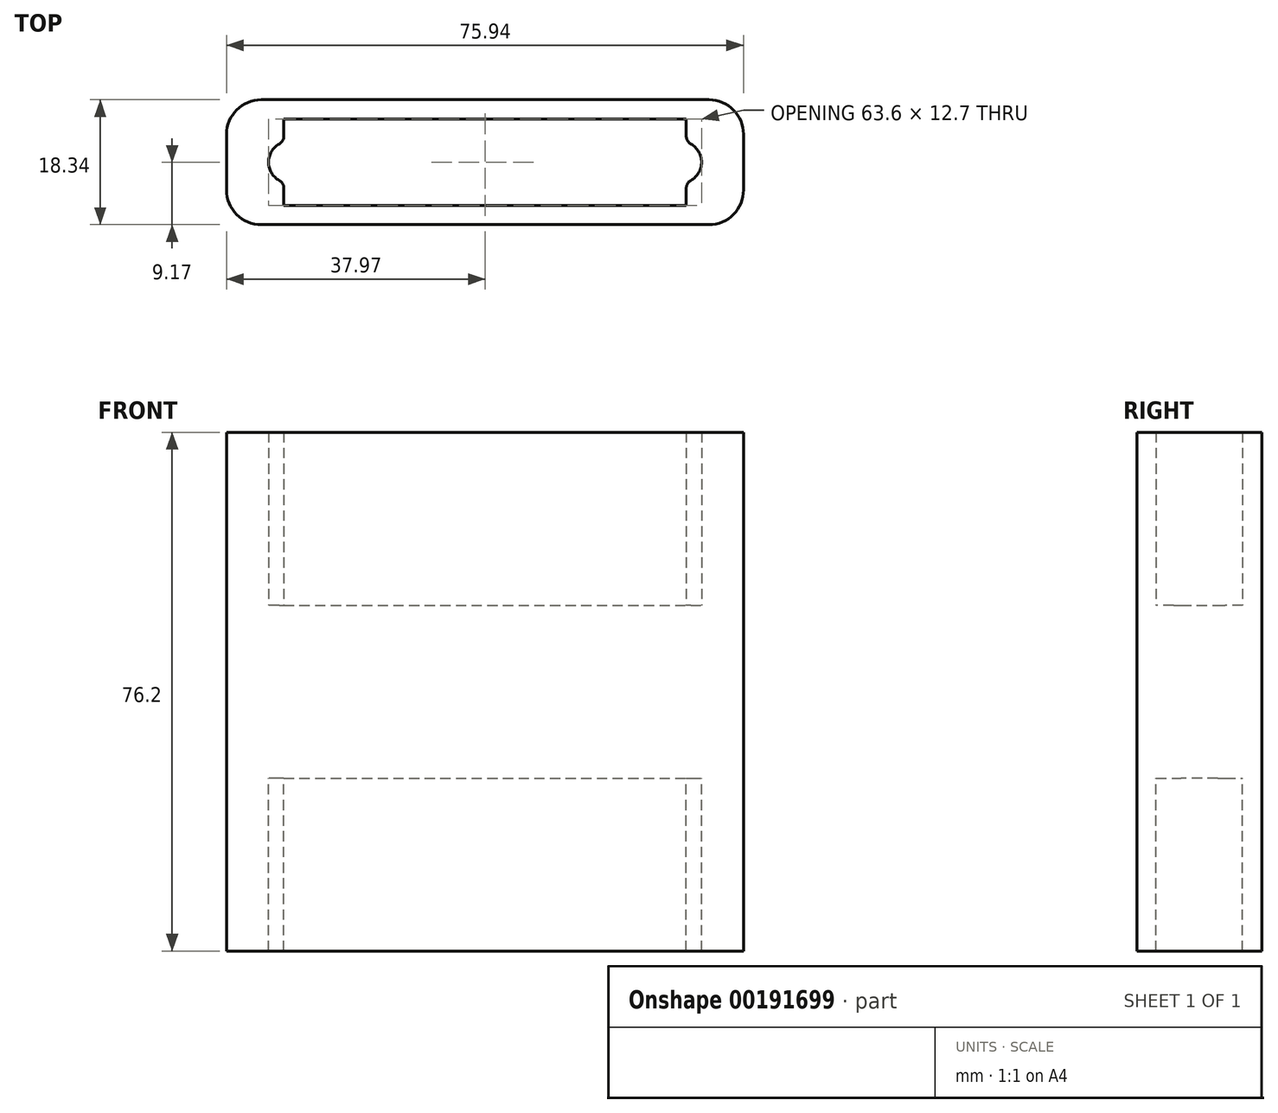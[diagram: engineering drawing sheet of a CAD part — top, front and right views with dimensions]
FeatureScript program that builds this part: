
annotation { "Feature Type Name" : "Feature", "Feature Type Description" : "" }
export const myFeature = defineFeature(function(context is Context, id is Id, definition is map)
    precondition{}
    {
        {
            var Q0;
            Q0=qCreatedBy(makeId("Top.planeOp"),FACE);
            var sketch = newSketch(context, id + "F0", { "sketchPlane" : qUnion([Q0])});
            skLineSegment(sketch, "E0.bottom", {"start": v(-37.97, 9.17) * mm, "end": v(37.97, 9.17) * mm});
            skLineSegment(sketch, "E0.top", {"start": v(-37.97, -9.17) * mm, "end": v(37.97, -9.17) * mm});
            skLineSegment(sketch, "E0.left", {"start": v(-37.97, 9.17) * mm, "end": v(-37.97, -9.17) * mm});
            skLineSegment(sketch, "E0.right", {"start": v(37.97, 9.17) * mm, "end": v(37.97, -9.17) * mm});
            skSolve(sketch);
        }
        {
            var Q0;
            Q0 = qSketchRegion(id + "F0", true);
            extrude(context, id + "F1", {"entities" : qUnion([Q0]), "endBound" : BoundingType.SYMMETRIC, "depth" : 25.4 * mm});
        }
        {
            var Q0;
            Q0=makeQuery(id+"F1.opExtrude","CAP_FACE",FACE,{"disambiguationData":[OSD([sQuery(id+"F0.wireOp",EDGE,"E0.bottom"),sQuery(id+"F0.wireOp",EDGE,"E0.top"),sQuery(id+"F0.wireOp",EDGE,"E0.left"),sQuery(id+"F0.wireOp",EDGE,"E0.right")])],"isStart":false});
            var sketch = newSketch(context, id + "F2", { "sketchPlane" : qUnion([Q0])});
            skLineSegment(sketch, "E1.bottom", {"start": v(-29.57, 6.35) * mm, "end": v(29.57, 6.35) * mm});
            skLineSegment(sketch, "E1.top", {"start": v(-29.57, -6.35) * mm, "end": v(29.57, -6.35) * mm});
            skLineSegment(sketch, "E1.left", {"start": v(-29.57, 6.35) * mm, "end": v(-29.57, 2.96) * mm});
            skLineSegment(sketch, "E1.right", {"start": v(29.57, 6.35) * mm, "end": v(29.57, 2.96) * mm});
            skPoint(sketch, "E2", {"position": v(-28.73, 0) * mm});
            skArc(sketch, "E3", {"start": v(-29.57, 2.96) * mm, "mid": v(-31.8, 0) * mm, "end": v(-29.57, -2.96) * mm});
            skLineSegment(sketch, "E4.trimOffspring", {"start": v(-29.57, -2.96) * mm, "end": v(-29.57, -6.35) * mm});
            skPoint(sketch, "E5", {"position": v(28.73, 0) * mm});
            skPoint(sketch, "E5.positionSnap0", {"position": v(29.57, 0) * mm});
            skArc(sketch, "E6", {"start": v(29.57, -2.96) * mm, "mid": v(31.8, 0) * mm, "end": v(29.57, 2.96) * mm});
            skLineSegment(sketch, "E7.trimOffspring", {"start": v(29.57, -2.96) * mm, "end": v(29.57, -6.35) * mm});
            skSolve(sketch);
        }
        {
            var Q0;
            Q0=makeQuery(id+"F1.opExtrude","CAP_FACE",FACE,{"disambiguationData":[OSD([sQuery(id+"F0.wireOp",EDGE,"E0.bottom"),sQuery(id+"F0.wireOp",EDGE,"E0.top"),sQuery(id+"F0.wireOp",EDGE,"E0.left"),sQuery(id+"F0.wireOp",EDGE,"E0.right")])],"isStart":true});
            var sketch = newSketch(context, id + "F3", { "sketchPlane" : qUnion([Q0])});
            skLineSegment(sketch, "E8.bottom", {"start": v(-29.57, 6.35) * mm, "end": v(29.57, 6.35) * mm});
            skLineSegment(sketch, "E8.top", {"start": v(-29.57, -6.35) * mm, "end": v(29.57, -6.35) * mm});
            skLineSegment(sketch, "E8.left", {"start": v(-29.57, 6.35) * mm, "end": v(-29.57, 2.96) * mm});
            skLineSegment(sketch, "E8.right", {"start": v(29.57, 6.35) * mm, "end": v(29.57, 2.96) * mm});
            skPoint(sketch, "E9", {"position": v(-28.73, 0) * mm});
            skArc(sketch, "E10", {"start": v(-29.57, 2.96) * mm, "mid": v(-31.8, 0) * mm, "end": v(-29.57, -2.96) * mm});
            skLineSegment(sketch, "E11.trimOffspring", {"start": v(-29.57, -2.96) * mm, "end": v(-29.57, -6.35) * mm});
            skPoint(sketch, "E12", {"position": v(28.73, 0) * mm});
            skPoint(sketch, "E12.positionSnap0", {"position": v(29.57, 0) * mm});
            skArc(sketch, "E13", {"start": v(29.57, -2.96) * mm, "mid": v(31.8, 0) * mm, "end": v(29.57, 2.96) * mm});
            skLineSegment(sketch, "E14.trimOffspring", {"start": v(29.57, -2.96) * mm, "end": v(29.57, -6.35) * mm});
            skSolve(sketch);
        }
        {
            var Q0;
            Q0=makeQuery(id+"F2.imprint","IMPRINT",FACE,{"disambiguationData":[TD([[makeQuery(id+"F2.imprint","IMPRINT",EDGE,{"derivedFrom":sQuery(id+"F2.wireOp",EDGE,"E1.bottom")}),1.0]])]});
            extrude(context, id + "F4", {"entities" : qUnion([Q0]), "operationType" : NewBodyOperationType.ADD, "depth" : 25.4 * mm});
        }
        {
            var Q0;
            Q0=makeQuery(id+"F3.imprint","IMPRINT",FACE,{"disambiguationData":[TD([[makeQuery(id+"F3.imprint","IMPRINT",EDGE,{"derivedFrom":sQuery(id+"F3.wireOp",EDGE,"E8.bottom")}),1.0]])]});
            extrude(context, id + "F5", {"entities" : qUnion([Q0]), "operationType" : NewBodyOperationType.ADD, "depth" : 25.4 * mm});
        }
        {
            var Q0;
            Q0=makeQuery(id+"F4.opExtrude","SWEPT_EDGE",EDGE,{"disambiguationData":[OSD([sQuery(id+"F2.wireOp",EDGE,"E1.left"),sQuery(id+"F2.wireOp",EDGE,"E3")])]});
            var Q1;
            Q1=makeQuery(id+"F4.opExtrude","SWEPT_EDGE",EDGE,{"disambiguationData":[OSD([sQuery(id+"F2.wireOp",EDGE,"E3"),sQuery(id+"F2.wireOp",EDGE,"E4.trimOffspring")])]});
            var Q2;
            Q2=makeQuery(id+"F4.opExtrude","SWEPT_EDGE",EDGE,{"disambiguationData":[OSD([sQuery(id+"F2.wireOp",EDGE,"E6"),sQuery(id+"F2.wireOp",EDGE,"E7.trimOffspring")])]});
            var Q3;
            Q3=makeQuery(id+"F4.opExtrude","SWEPT_EDGE",EDGE,{"disambiguationData":[OSD([sQuery(id+"F2.wireOp",EDGE,"E1.right"),sQuery(id+"F2.wireOp",EDGE,"E6")])]});
            var Q4;
            Q4=makeQuery(id+"F5.opExtrude","SWEPT_EDGE",EDGE,{"disambiguationData":[OSD([sQuery(id+"F3.wireOp",EDGE,"E8.left"),sQuery(id+"F3.wireOp",EDGE,"E10")])]});
            var Q5;
            Q5=makeQuery(id+"F5.opExtrude","SWEPT_EDGE",EDGE,{"disambiguationData":[OSD([sQuery(id+"F3.wireOp",EDGE,"E10"),sQuery(id+"F3.wireOp",EDGE,"E11.trimOffspring")])]});
            var Q6;
            Q6=makeQuery(id+"F5.opExtrude","SWEPT_EDGE",EDGE,{"disambiguationData":[OSD([sQuery(id+"F3.wireOp",EDGE,"E13"),sQuery(id+"F3.wireOp",EDGE,"E14.trimOffspring")])]});
            var Q7;
            Q7=makeQuery(id+"F5.opExtrude","SWEPT_EDGE",EDGE,{"disambiguationData":[OSD([sQuery(id+"F3.wireOp",EDGE,"E8.right"),sQuery(id+"F3.wireOp",EDGE,"E13")])]});
            fillet(context, id + "F6", {"entities" : qUnion([Q0, Q1, Q2, Q3, Q4, Q5, Q6, Q7]), "radius" : 1.27 * mm, "tangentPropagation" : true, "allowEdgeOverflow" : false});
        }
        {
            var Q0;
            {var subQ0=sQuery(id+"F0.wireOp",EDGE,"E0.right");var subQ1=sQuery(id+"F0.wireOp",EDGE,"E0.top");Q0=makeQuery(id+"F5.boolean.opBoolean","MERGE",EDGE,{"derivedFrom":[makeQuery(id+"F4.boolean.opBoolean","MERGE",EDGE,{"derivedFrom":[makeQuery(id+"F1.opExtrude","SWEPT_EDGE",EDGE,{"disambiguationData":[OSD([subQ1,subQ0])]}),makeQuery(id+"F4.opExtrude","SWEPT_EDGE",EDGE,{"disambiguationData":[OSD([subQ1,subQ0])]})]}),makeQuery(id+"F5.opExtrude","SWEPT_EDGE",EDGE,{"disambiguationData":[OSD([subQ1,subQ0])]})]});}
            var Q1;
            {var subQ0=sQuery(id+"F0.wireOp",EDGE,"E0.right");var subQ1=sQuery(id+"F0.wireOp",EDGE,"E0.bottom");Q1=makeQuery(id+"F5.boolean.opBoolean","MERGE",EDGE,{"derivedFrom":[makeQuery(id+"F4.boolean.opBoolean","MERGE",EDGE,{"derivedFrom":[makeQuery(id+"F1.opExtrude","SWEPT_EDGE",EDGE,{"disambiguationData":[OSD([subQ1,subQ0])]}),makeQuery(id+"F4.opExtrude","SWEPT_EDGE",EDGE,{"disambiguationData":[OSD([subQ1,subQ0])]})]}),makeQuery(id+"F5.opExtrude","SWEPT_EDGE",EDGE,{"disambiguationData":[OSD([subQ1,subQ0])]})]});}
            var Q2;
            {var subQ0=sQuery(id+"F0.wireOp",EDGE,"E0.left");var subQ1=sQuery(id+"F0.wireOp",EDGE,"E0.top");Q2=makeQuery(id+"F5.boolean.opBoolean","MERGE",EDGE,{"derivedFrom":[makeQuery(id+"F4.boolean.opBoolean","MERGE",EDGE,{"derivedFrom":[makeQuery(id+"F1.opExtrude","SWEPT_EDGE",EDGE,{"disambiguationData":[OSD([subQ1,subQ0])]}),makeQuery(id+"F4.opExtrude","SWEPT_EDGE",EDGE,{"disambiguationData":[OSD([subQ1,subQ0])]})]}),makeQuery(id+"F5.opExtrude","SWEPT_EDGE",EDGE,{"disambiguationData":[OSD([subQ1,subQ0])]})]});}
            var Q3;
            {var subQ0=sQuery(id+"F0.wireOp",EDGE,"E0.left");var subQ1=sQuery(id+"F0.wireOp",EDGE,"E0.bottom");Q3=makeQuery(id+"F5.boolean.opBoolean","MERGE",EDGE,{"derivedFrom":[makeQuery(id+"F4.boolean.opBoolean","MERGE",EDGE,{"derivedFrom":[makeQuery(id+"F1.opExtrude","SWEPT_EDGE",EDGE,{"disambiguationData":[OSD([subQ1,subQ0])]}),makeQuery(id+"F4.opExtrude","SWEPT_EDGE",EDGE,{"disambiguationData":[OSD([subQ1,subQ0])]})]}),makeQuery(id+"F5.opExtrude","SWEPT_EDGE",EDGE,{"disambiguationData":[OSD([subQ1,subQ0])]})]});}
            fillet(context, id + "F7", {"entities" : qUnion([Q0, Q1, Q2, Q3]), "radius" : 5.08 * mm, "tangentPropagation" : true, "allowEdgeOverflow" : false});
        }
    });
